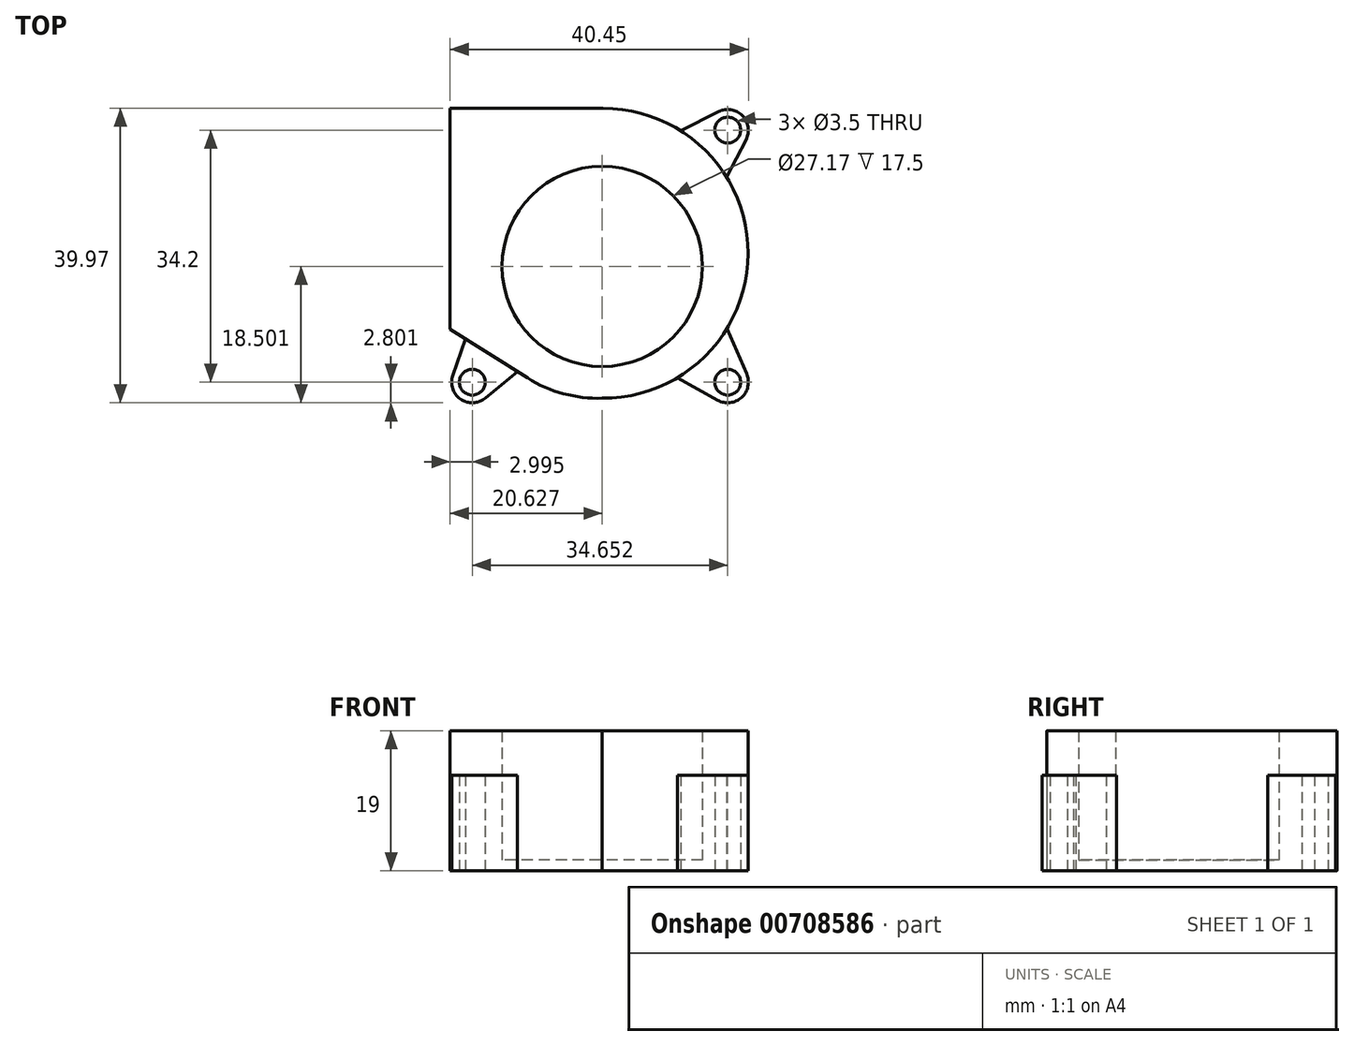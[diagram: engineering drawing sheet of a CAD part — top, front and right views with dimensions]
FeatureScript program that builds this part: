
annotation { "Feature Type Name" : "Feature", "Feature Type Description" : "" }
export const myFeature = defineFeature(function(context is Context, id is Id, definition is map)
    precondition{}
    {
        {
            var Q0;
            Q0=qCreatedBy(makeId("Top.planeOp"),FACE);
            var sketch = newSketch(context, id + "F0", { "sketchPlane" : qUnion([Q0])});
            skLineSegment(sketch, "E0", {"start": v(22.56, 24.56) * mm, "end": v(22.56, -5.44) * mm});
            skCircle(sketch, "E1", {"center": v(43.19, 3.1) * mm, "radius": 13.59 * mm});
            skCircle(sketch, "E2", {"center": v(60.2, 21.6) * mm, "radius": 1.75 * mm});
            skCircle(sketch, "E3", {"center": v(60.2, -12.6) * mm, "radius": 1.75 * mm});
            skCircle(sketch, "E4", {"center": v(25.55, -12.6) * mm, "radius": 1.75 * mm});
            skLineSegment(sketch, "E5", {"start": v(22.56, 24.56) * mm, "end": v(43.3, 24.56) * mm});
            skArc(sketch, "E6", {"start": v(43.19, -14.78) * mm, "mid": v(62.96, 4.83) * mm, "end": v(43.3, 24.56) * mm});
            skArc(sketch, "E7", {"start": v(33.06, -12.05) * mm, "mid": v(37.92, -14.17) * mm, "end": v(43.19, -14.78) * mm});
            skLineSegment(sketch, "E8", {"start": v(22.56, -5.44) * mm, "end": v(33.06, -12.05) * mm});
            skLineSegment(sketch, "E9", {"start": v(53.8, 21.5) * mm, "end": v(58.95, 24.1) * mm});
            skLineSegment(sketch, "E10", {"start": v(60.05, 15.19) * mm, "end": v(62.7, 20.3) * mm});
            skArc(sketch, "E11", {"start": v(62.7, 20.3) * mm, "mid": v(62.2, 23.56) * mm, "end": v(58.95, 24.1) * mm});
            skLineSegment(sketch, "E12", {"start": v(15.95, 3.1) * mm, "end": v(74, 3.1) * mm, "construction": true});
            skLineSegment(sketch, "E13", {"start": v(43.08, 27.19) * mm, "end": v(43.3, -21.13) * mm, "construction": true});
            skArc(sketch, "E14", {"start": v(22.91, -11.68) * mm, "mid": v(23.95, -14.9) * mm, "end": v(27.33, -14.77) * mm});
            skArc(sketch, "E15", {"start": v(58.85, -15.06) * mm, "mid": v(62.1, -14.68) * mm, "end": v(62.77, -11.49) * mm});
            skLineSegment(sketch, "E16", {"start": v(22.91, -11.68) * mm, "end": v(24.64, -6.75) * mm});
            skLineSegment(sketch, "E17", {"start": v(27.33, -14.77) * mm, "end": v(31.7, -11.2) * mm});
            skLineSegment(sketch, "E18", {"start": v(53.37, -12) * mm, "end": v(58.85, -15.06) * mm});
            skLineSegment(sketch, "E19", {"start": v(60.09, -5.35) * mm, "end": v(62.77, -11.49) * mm});
            skSolve(sketch);
        }
        {
            var Q0;
            {var subQ7=sQuery(id+"F0.wireOp",EDGE,"E0");Q0=makeQuery(id+"F0.imprint","IMPRINT",FACE,{"disambiguationData":[TD([[makeQuery(id+"F0.imprint","IMPRINT",EDGE,{"derivedFrom":subQ7}),1.0]])]});}
            var Q1;
            Q1=makeQuery(id+"F0.imprint","IMPRINT",FACE,{"disambiguationData":[TD([[makeQuery(id+"F0.imprint","IMPRINT",EDGE,{"derivedFrom":sQuery(id+"F0.wireOp",EDGE,"E1")}),1.0]])]});
            var Q2;
            Q2=makeQuery(id+"F0.imprint","IMPRINT",FACE,{"disambiguationData":[TD([[makeQuery(id+"F0.imprint","IMPRINT",EDGE,{"derivedFrom":sQuery(id+"F0.wireOp",EDGE,"E4")}),-1.0]])]});
            var Q3;
            Q3=makeQuery(id+"F0.imprint","IMPRINT",FACE,{"disambiguationData":[TD([[makeQuery(id+"F0.imprint","IMPRINT",EDGE,{"derivedFrom":sQuery(id+"F0.wireOp",EDGE,"E3")}),-1.0]])]});
            var Q4;
            Q4=makeQuery(id+"F0.imprint","IMPRINT",FACE,{"disambiguationData":[TD([[makeQuery(id+"F0.imprint","IMPRINT",EDGE,{"derivedFrom":sQuery(id+"F0.wireOp",EDGE,"E2")}),-1.0]])]});
            extrude(context, id + "F1", {"entities" : qUnion([Q0, Q1, Q2, Q3, Q4]), "depth" : 1.5 * mm, "offsetDistance" : 25 * mm});
        }
        {
            var Q0;
            Q0=makeQuery(id+"F0.imprint","IMPRINT",FACE,{"disambiguationData":[TD([[makeQuery(id+"F0.imprint","IMPRINT",EDGE,{"derivedFrom":sQuery(id+"F0.wireOp",EDGE,"E4")}),-1.0]])]});
            var Q1;
            Q1=makeQuery(id+"F0.imprint","IMPRINT",FACE,{"disambiguationData":[TD([[makeQuery(id+"F0.imprint","IMPRINT",EDGE,{"derivedFrom":sQuery(id+"F0.wireOp",EDGE,"E3")}),-1.0]])]});
            var Q2;
            Q2=makeQuery(id+"F0.imprint","IMPRINT",FACE,{"disambiguationData":[TD([[makeQuery(id+"F0.imprint","IMPRINT",EDGE,{"derivedFrom":sQuery(id+"F0.wireOp",EDGE,"E2")}),-1.0]])]});
            extrude(context, id + "F2", {"entities" : qUnion([Q0, Q1, Q2]), "operationType" : NewBodyOperationType.ADD, "depth" : 13 * mm, "offsetDistance" : 25 * mm});
        }
        {
            var Q0;
            {var subQ7=sQuery(id+"F0.wireOp",EDGE,"E0");Q0=makeQuery(id+"F0.imprint","IMPRINT",FACE,{"disambiguationData":[TD([[makeQuery(id+"F0.imprint","IMPRINT",EDGE,{"derivedFrom":subQ7}),1.0]])]});}
            extrude(context, id + "F3", {"entities" : qUnion([Q0]), "operationType" : NewBodyOperationType.ADD, "depth" : 19 * mm, "offsetDistance" : 25 * mm});
        }
    });
